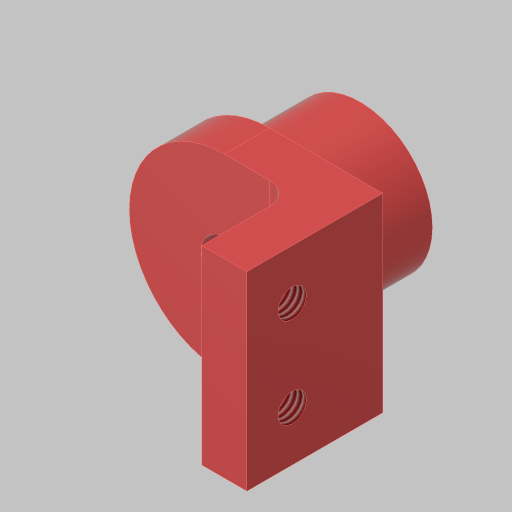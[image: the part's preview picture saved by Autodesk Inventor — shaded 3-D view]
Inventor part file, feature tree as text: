
AUTODESK INVENTOR PART (.ipt)
format: ipt  version: 2023.5 (Build 275446000, 446)  size: 151,040 bytes
history: native  units: in
note: dims shown in document units (in); Inventor stores cm internally (conversion verified against a paired STEP export)
features: sketch x5, extrude x3, hole x2, fillet x1, projected_geometry x1
ambient origin geometry x8: Origin, YZ Plane, XZ Plane, XY Plane, X Axis, Y Axis, Z Axis, Center Point
bodies: Solid1 (feature_tree)
feature tree (12):
  extrude  "Extrusion1"  Depth=0.5in TaperAngle=0.0deg
  extrude  "Extrusion2"  Depth=0.25in TaperAngle=0.0deg
  hole  "Hole2"  [1 undecoded]
  extrude  "Extrusion3"  Depth=0.25in
  fillet  "Fillet1"  Radius=0.5in
  hole  "Hole3"  [1 undecoded]
  sketch  "Sketch1"  dims[d0=0.8in d1=0.5in d2=0.0in]
  sketch  "Sketch2"  dims[d3=0.125in d4=0.25in d5=0.0in]
  sketch  "Sketch4"  dims[d6=0.688in d14=0.625in]
  sketch  "Sketch5"  dims[d15=0.257in d16=0.75in d17=0.375in d18=0.25in d19=0.5635in d20=1.0in d21=0.8108in d22=0.25in d23=0.5in d24=0.0in]
  sketch  "Sketch6"  dims[d25=0.125in d26=0.5in d27=0.156in d28=0.38in d29=0.385in d30=0.25in d31=0.5635in d32=1.0in d33=0.8108in d34=0.25in]
  projected_geometry  "Project Cut Edges1"
note: 2 required parameter values undecoded (feature->parameter linkage not recoverable at this tier; creation-order binding heuristic only, values carry confidence <= 0.55)
